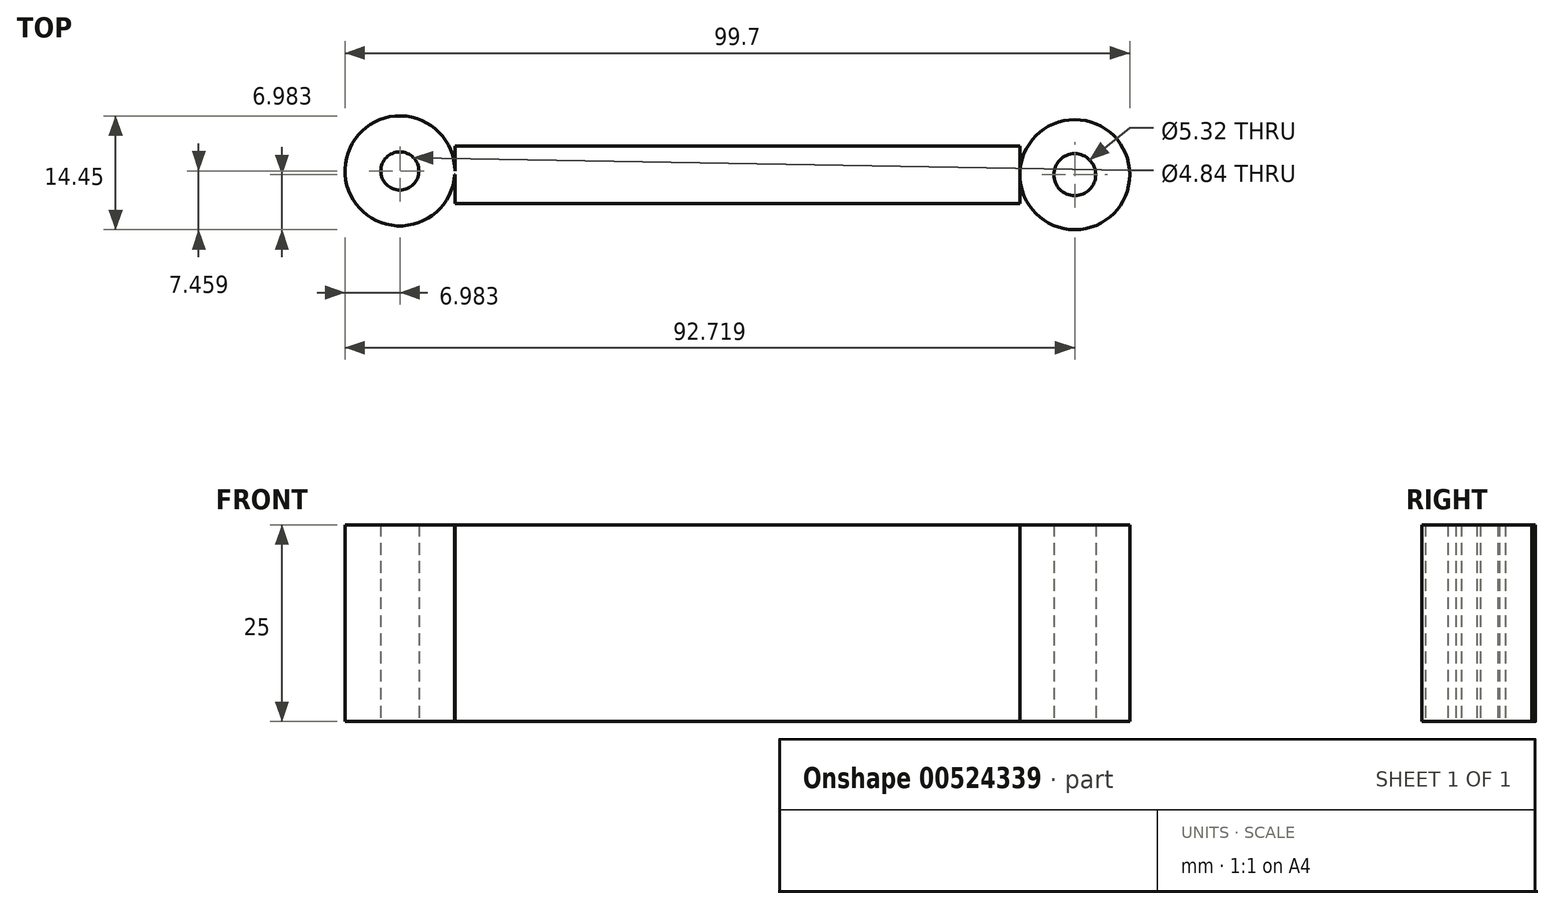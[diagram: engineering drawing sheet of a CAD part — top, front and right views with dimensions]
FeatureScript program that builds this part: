
annotation { "Feature Type Name" : "Feature", "Feature Type Description" : "" }
export const myFeature = defineFeature(function(context is Context, id is Id, definition is map)
    precondition{}
    {
        {
            var Q0;
            Q0=qCreatedBy(makeId("Top.planeOp"),FACE);
            var sketch = newSketch(context, id + "F0", { "sketchPlane" : qUnion([Q0])});
            skLineSegment(sketch, "E0", {"start": v(-27, 12.06) * mm, "end": v(44.77, 12.06) * mm});
            skLineSegment(sketch, "E1", {"start": v(44.77, 12.06) * mm, "end": v(44.77, 4.76) * mm});
            skLineSegment(sketch, "E2", {"start": v(44.77, 4.76) * mm, "end": v(-27, 4.76) * mm});
            skLineSegment(sketch, "E3", {"start": v(-27, 4.76) * mm, "end": v(-27, 12.06) * mm});
            skCircle(sketch, "E4", {"center": v(-33.98, 8.89) * mm, "radius": 6.99 * mm});
            skCircle(sketch, "E5", {"center": v(51.76, 8.41) * mm, "radius": 6.99 * mm});
            skPoint(sketch, "E5.centerSnap0", {"position": v(44.77, 8.41) * mm});
            skCircle(sketch, "E6", {"center": v(-33.98, 8.89) * mm, "radius": 2.42 * mm});
            skCircle(sketch, "E7", {"center": v(51.76, 8.41) * mm, "radius": 2.66 * mm});
            skLineSegment(sketch, "E8", {"start": v(44.77, 8.41) * mm, "end": v(-27, 8.41) * mm});
            skLineSegment(sketch, "E9", {"start": v(-27, 8.41) * mm, "end": v(44.77, 8.41) * mm});
            skSolve(sketch);
        }
        {
            var Q0;
            {var subQ0=sQuery(id+"F0.wireOp",EDGE,"E9");var subQ1=sQuery(id+"F0.wireOp",EDGE,"E3");var subQ2=makeQuery(id+"F0.imprint","INTERSECT",VERTEX,{"derivedFrom":[subQ1,subQ0]});Q0=makeQuery(id+"F0.imprint","IMPRINT",FACE,{"disambiguationData":[TD([[makeQuery(id+"F0.imprint","IMPRINT",EDGE,{"disambiguationData":[TD([[subQ2,-1.0]])],"derivedFrom":subQ1}),1.0]])]});}
            var Q1;
            {var subQ1=sQuery(id+"F0.wireOp",EDGE,"E0");Q1=makeQuery(id+"F0.imprint","IMPRINT",FACE,{"disambiguationData":[TD([[makeQuery(id+"F0.imprint","IMPRINT",EDGE,{"derivedFrom":subQ1}),-1.0]])]});}
            var Q2;
            {var subQ0=sQuery(id+"F0.wireOp",EDGE,"E2");Q2=makeQuery(id+"F0.imprint","IMPRINT",FACE,{"disambiguationData":[TD([[makeQuery(id+"F0.imprint","IMPRINT",EDGE,{"derivedFrom":subQ0}),-1.0]])]});}
            extrude(context, id + "F1", {"entities" : qUnion([Q0, Q1, Q2]), "depth" : 3 * mm, "offsetDistance" : 25 * mm});
        }
        {
            var Q0;
            Q0 = qSketchRegion(id + "F0", true);
            extrude(context, id + "F2", {"entities" : qUnion([Q0]), "operationType" : NewBodyOperationType.ADD, "depth" : 25 * mm, "offsetDistance" : 25 * mm});
        }
    });
